# Revit family: TY-B-TY1251_Imperial
name_source: partatom
category: Sprinklers
units: mm (PartAtom-declared; Revit-internal decimal feet)

## family parameters
Always vertical = Yes
Cut with Voids When Loaded = No
Maintain Annotation Orientation = No
OmniClass Number = 23.65.70.17.11.24
OmniClass Title = Fire Fighting Sprinkler Heads
Part Type = Normal
Room Calculation Point = No
Round Connector Dimension = Use Diameter
Shared = No
Work Plane-Based = No

## types (18) — shared parameters
COBie = Yes
COBie.Component.Name = Sprinklers:Pendent_SIN
COBie.Type = Yes
COBie.Type.AssetType = Fixed
COBie.Type.Category = Pr_70_55_97_84:Sprinklers
COBie.Type.DurationUnit = year
COBie.Type.Manufacturer = Tyco Fire Protection Products
COBie.Type.Material = Bronze
COBie.Type.NominalHeight = 0' - 0"
COBie.Type.NominalLength = 0' - 0"
COBie.Type.NominalWidth = 0' - 0"
COBie.Type.Shape = Cylinder
COBie.Type.Size = 1/2"(DN15)
COBie.Type.WarrantyGuarantorParts = http://tycofsbp.com
TFPPTerms_of_Sale.pdf
Coverage = Standard
Coverage_ = Standard
Default Elevation = 0' - 0"
K-Factor = 2.7954
Manufacturer = Tyco Fire Protection Products
Manufacturer URL = www.tyco-fire.com
Material_ = Bronze
Model = TY-B
Nominal Diameter 1 = 1"
Orifice = Standard
Orifice Size = 0"
Outside Diameter 1 = 1"
Response = Standard
SIN No = TY1251
Takeout 1 = 2"
Technical Data Sheet No = TFP151
zero-valued in all types: COBie.Type.ReplacementCost, Style Id

## per-type parameters (varying)
| type | COBie.Component.Description | COBie.Component.InstallationDate | COBie.Type.Colour | COBie.Type.Finish | COBie.Type.ModelNumber | COBie.Type.ModelReference | COBie.Type.WarrantyDurationUnit | Description | Finish_ | Part No | Response_ | Temperature Rating |
| Pendent ½" NPT 135°F Brass_57-531-1-135 | TY-B Wet Pendent  135°F K2.8 1/2 NPT Br |  | Brass | Natural Brass | 57-531-1-135 | TY-B Wet Pendent  135°F K2.8 1/2 NPT Br |  | TY-B Pendent Brass 135°F 2.8K ½" NPT | Natural Brass | 57-531-1-135 | Standard | 135 °F |
| Pendent ½" NPT 155°F Brass_57-531-1-155 | TY-B Wet Pendent  155°F K2.8 1/2 NPT Br |  | Brass | Natural Brass | 57-531-1-155 | TY-B Wet Pendent  155°F K2.8 1/2 NPT Br |  | TY-B Pendent Brass 155°F 2.8K ½" NPT | Natural Brass | 57-531-1-155 | Standard | 155 °F |
| Pendent ½" NPT 175°F Brass_57-531-1-175 | TY-B Wet Pendent  175°F K2.8 1/2 NPT Br |  | Brass | Natural Brass | 57-531-1-175 | TY-B Wet Pendent  175°F K2.8 1/2 NPT Br |  | TY-B Pendent Brass 79°C 2.8K ½" NPT | Natural Brass | 57-531-1-175 | Standard | 175 °F |
| Pendent ½" NPT 200°F Brass_57-531-1-200 | TY-B Wet Pendent  200°F K2.8 1/2 NPT Br | n/ | Brass | Natural Brass | 57-531-1-200 | TY-B Wet Pendent  200°F K2.8 1/2 NPT Br |  | TY-B Pendent Brass 200°F 2.8K ½" NPT | Natural Brass | 57-531-1-200 | Standard | 200 °F |
| Pendent ½" NPT 286°F Brass_57-531-1-286 | TY-B Wet Pendent  286°F K2.8 1/2 NPT Br |  | Brass | Natural Brass | 57-531-1-286 | TY-B Wet Pendent  286°F K2.8 1/2 NPT Br |  | TY-B Pendent Brass 286°F 2.8K ½" NPT | Natural Brass | 57-531-1-286 | Standard | 286 °F |
| Pendent ½" NPT 360°F Brass_57-531-1-360 | TY-B Wet Pendent  360°F K2.8 1/2 NPT Br |  | Brass | Natural Brass | 57-531-1-360 | TY-B Wet Pendent  360°F K2.8 1/2 NPT Br |  | TY-B Pendent Brass 360°F 2.8K ½" NPT | Natural Brass | 57-531-1-360 | Standard | 360 °F |
| Pendent ½" NPT 135°F White_57-531-3-135 | TY-B Wet Pendent  135°F K2.8 1/2 NPT Wh9010 |  | White | Pure White | 57-531-3-135 | TY-B Wet Pendent  135°F K2.8 1/2 NPT Wh9010 |  | TY-B Pendent White 135°F 2.8K ½" NPT | White RAL9010 | 57-531-3-135 | Standard | 135 °F |
| Pendent ½" NPT 155°F White_57-531-3-155 | TY-B Wet Pendent  155°F K2.8 1/2 NPT Wh9010 |  | White | Pure White | 57-531-3-155 | TY-B Wet Pendent  155°F K2.8 1/2 NPT Wh9010 |  | TY-B Pendent White 155°F 2.8K ½" NPT | White RAL9010 | 57-531-3-155 | Standard | 155 °F |
| Pendent ½" NPT 175°F White_57-531-3-175 | TY-B Wet Pendent  175°F K2.8 1/2 NPT Wh9010 |  | White | Pure White | 57-531-3-175 | TY-B Wet Pendent  175°F K2.8 1/2 NPT Wh9010 |  | TY-B Pendent White 175°F 2.8K ½" NPT | White RAL9010 | 57-531-3-175 | Standard | 175 °F |
| Pendent ½" NPT 200°F White_57-531-3-200 | TY-B Wet Pendent  200°F K2.8 1/2 NPT Wh9010 |  | White | Pure White | 57-531-3-200 | TY-B Wet Pendent  200°F K2.8 1/2 NPT Wh9010 |  | TY-B Pendent White 200°F 2.8K ½" NPT | White RAL9010 | 57-531-3-200 | Standard | 200 °F |
| Pendent ½" NPT 286°F White_57-531-3-286 | TY-B Wet Pendent  286°F K2.8 1/2 NPT Wh9010 |  | White | Pure White | 57-531-3-286 | TY-B Wet Pendent  286°F K2.8 1/2 NPT Wh9010 |  | TY-B Pendent White 286°F 2.8K ½" NPT | White RAL9010 | 57-531-3-286 | Standard | 286 °F |
| Pendent ½" NPT 360°F White_57-531-3-360 | TY-B Wet Pendent  360°F K2.8 1/2 NPT Wh9010 |  | White | Pure White | 57-531-3-360 | TY-B Wet Pendent  360°F K2.8 1/2 NPT Wh9010 |  | TY-B Pendent White 360°F 2.8K ½" NPT | White RAL9010 | 57-531-3-360 | Standard | 360 °F |
| Pendent ½" NPT 135°F Chrome_57-531-9-135 | TY-B Wet Pendent  135°F K2.8 1/2 NPT Chr |  | Silver | Chrome Plated | 57-531-9-135 | TY-B Wet Pendent  135°F K2.8 1/2 NPT Chr |  | TY-B Pendent Chrome 135°F 2.8K ½" NPT | Chrome Plated | 57-531-9-135 | Standard | 135 °F |
| Pendent ½" NPT 155°F Chrome_57-531-9-155 | TY-B Wet Pendent  155°F K2.8 1/2 NPT Chr |  | Silver | Chrome Plated | 57-531-9-155 | TY-B Wet Pendent  155°F K2.8 1/2 NPT Chr |  | TY-B Pendent Chrome 155°F 2.8K ½" NPT | Chrome Plated | 57-531-9-155 | Stnadard | 155 °F |
| Pendent ½" NPT 175°F Chrome_57-531-9-175 | TY-B Wet Pendent  175°F K2.8 1/2 NPT Chr |  | Gray | Chrome Plated | 57-531-9-175 | TY-B Wet Pendent  175°F K2.8 1/2 NPT Chr | year | TY-B Pendent Chrome 175°F 2.8K ½" NPT | Chrome Plated | 57-531-9-175 | Standard | 175 °F |
| Pendent ½" NPT 200°F Chrome_57-531-9-200 | TY-B Wet Pendent  200°F K2.8 1/2 NPT Chr |  | Silver | Chrome Plated | 57-531-9-200 | TY-B Wet Pendent  200°F K2.8 1/2 NPT Chr |  | TY-B Pendent Chrome 200°F 2.8K ½" NPT | Chrome Plated | 57-531-9-200 | Standard | 200 °F |
| Pendent  ½" NPT 286°F Chrome_57-531-9-286 | TY-B Wet Pendent  286°F K2.8 1/2 NPT Chr |  | Silver | Chrome plated | 57-531-9-286 | TY-B Wet Pendent  286°F K2.8 1/2 NPT Chr |  | TY-B Pendent Chrome 286°F 2.8K ½" NPT | Chrome Plated | 57-531-9-286 | Standard | 286 °F |
| Pendent ½" NPT 360°F Chrome_57-531-9-360 | TY-B Wet Pendent  360°F K2.8 1/2 NPT Chr |  | Silver | Chrome Plated | 57-531-9-360 | TY-B Wet Pendent  360°F K2.8 1/2 NPT Chr |  | TY-B Pendent Chrome 360°F 2.8K ½" NPT | Chrome Plated | 57-531-9-360 | Standard | 360 °F |

## geometry (parser evidence)
native form markers: Blend x2, Sweep x44
no freeform markers — native parametric forms only
